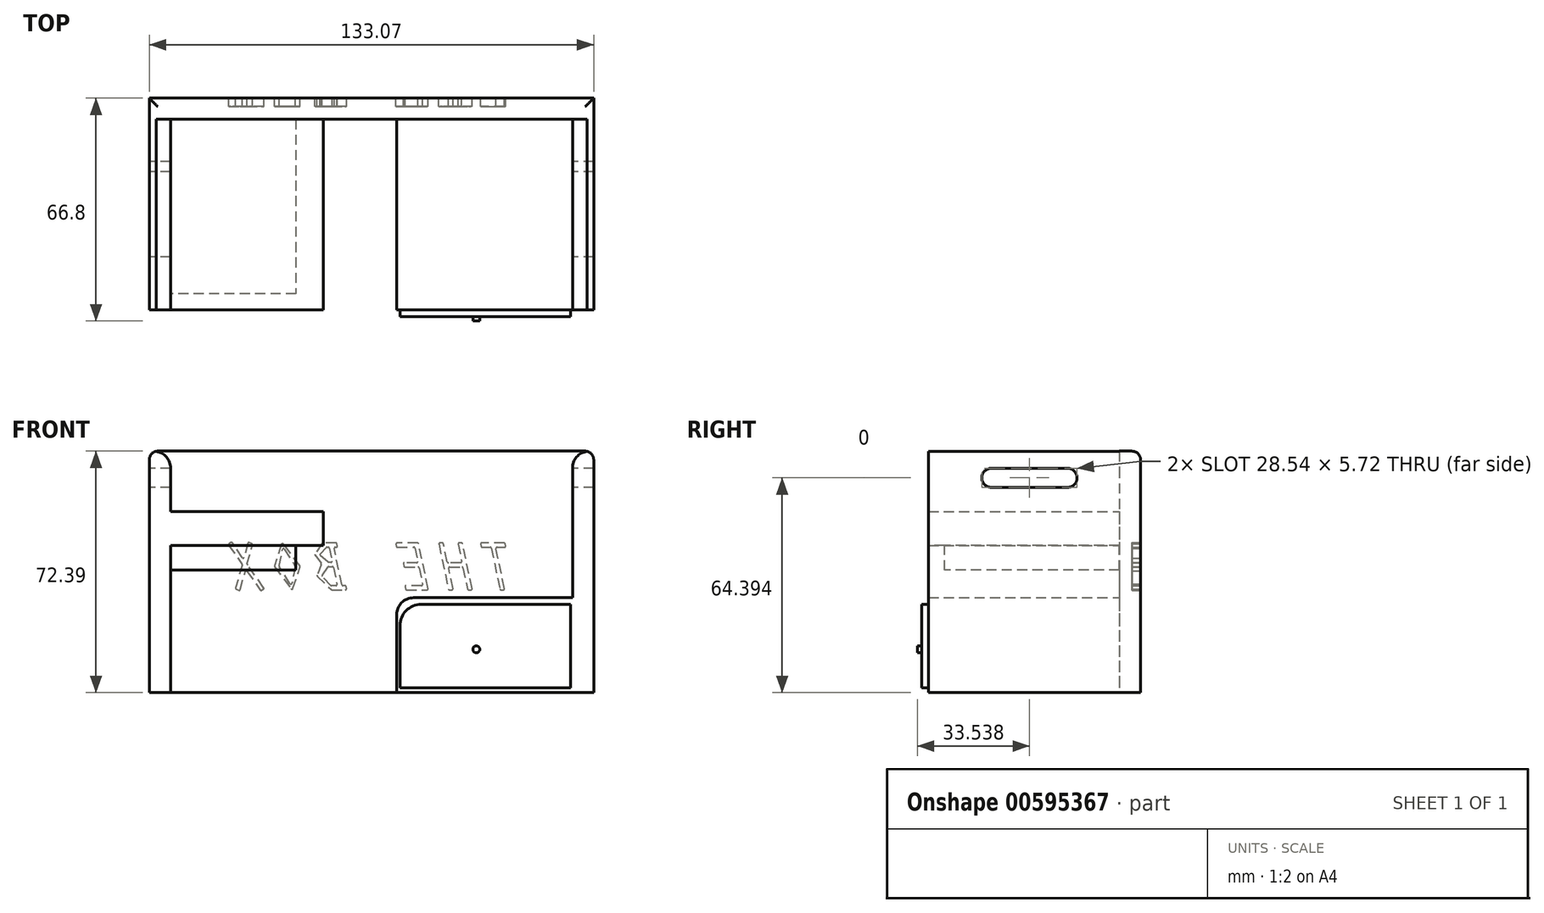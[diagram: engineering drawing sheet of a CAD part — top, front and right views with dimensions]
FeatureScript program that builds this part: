
annotation { "Feature Type Name" : "Feature", "Feature Type Description" : "" }
export const myFeature = defineFeature(function(context is Context, id is Id, definition is map)
    precondition{}
    {
        {
            var Q0;
            Q0=qCreatedBy(makeId("Top.planeOp"),FACE);
            var sketch = newSketch(context, id + "F0", { "sketchPlane" : qUnion([Q0])});
            skLineSegment(sketch, "E0", {"start": v(-65.97, -48.33) * mm, "end": v(-65.97, 15.17) * mm});
            skLineSegment(sketch, "E1", {"start": v(-65.97, 15.17) * mm, "end": v(67.1, 15.17) * mm});
            skLineSegment(sketch, "E2", {"start": v(67.1, 15.17) * mm, "end": v(67.1, -48.33) * mm});
            skLineSegment(sketch, "E3", {"start": v(67.1, -48.33) * mm, "end": v(60.75, -48.33) * mm});
            skLineSegment(sketch, "E4", {"start": v(60.75, -48.33) * mm, "end": v(60.75, 8.82) * mm});
            skLineSegment(sketch, "E5", {"start": v(60.75, 8.82) * mm, "end": v(-59.62, 8.82) * mm});
            skLineSegment(sketch, "E6", {"start": v(-59.62, 8.82) * mm, "end": v(-59.62, -48.33) * mm});
            skLineSegment(sketch, "E7", {"start": v(-59.62, -48.33) * mm, "end": v(-65.97, -48.33) * mm});
            skSolve(sketch);
        }
        {
            var Q0;
            Q0 = qSketchRegion(id + "F0", true);
            extrude(context, id + "F1", {"entities" : qUnion([Q0]), "depth" : 72.39 * mm, "offsetDistance" : 25.4 * mm});
        }
        {
            var Q0;
            Q0=makeQuery(id+"F1.opExtrude","SWEPT_FACE",FACE,{"disambiguationData":[OSD([sQuery(id+"F0.wireOp",EDGE,"E6")])]});
            var sketch = newSketch(context, id + "F2", { "sketchPlane" : qUnion([Q0])});
            skLineSegment(sketch, "E8.bottom", {"start": v(-48.33, 54.32) * mm, "end": v(8.82, 54.32) * mm});
            skLineSegment(sketch, "E8.top", {"start": v(-48.33, 44.07) * mm, "end": v(8.82, 44.07) * mm});
            skLineSegment(sketch, "E8.left", {"start": v(-48.33, 54.32) * mm, "end": v(-48.33, 44.07) * mm});
            skLineSegment(sketch, "E8.right", {"start": v(8.82, 54.32) * mm, "end": v(8.82, 44.07) * mm});
            skSolve(sketch);
        }
        {
            var Q0;
            Q0 = qSketchRegion(id + "F2", true);
            extrude(context, id + "F3", {"entities" : qUnion([Q0]), "operationType" : NewBodyOperationType.ADD, "depth" : 45.72 * mm, "offsetDistance" : 25.4 * mm});
        }
        {
            var Q0;
            Q0=makeQuery(id+"F1.opExtrude","CAP_FACE",FACE,{"disambiguationData":[OSD([sQuery(id+"F0.wireOp",EDGE,"E0"),sQuery(id+"F0.wireOp",EDGE,"E1"),sQuery(id+"F0.wireOp",EDGE,"E2"),sQuery(id+"F0.wireOp",EDGE,"E3"),sQuery(id+"F0.wireOp",EDGE,"E4"),sQuery(id+"F0.wireOp",EDGE,"E5"),sQuery(id+"F0.wireOp",EDGE,"E6"),sQuery(id+"F0.wireOp",EDGE,"E7")])],"isStart":true});
            var sketch = newSketch(context, id + "F4", { "sketchPlane" : qUnion([Q0])});
            skLineSegment(sketch, "E9.bottom", {"start": v(60.75, 48.33) * mm, "end": v(8.08, 48.33) * mm});
            skLineSegment(sketch, "E9.top", {"start": v(60.75, -8.82) * mm, "end": v(8.08, -8.82) * mm});
            skLineSegment(sketch, "E9.left", {"start": v(60.75, 48.33) * mm, "end": v(60.75, -8.82) * mm});
            skLineSegment(sketch, "E9.right", {"start": v(8.08, 48.33) * mm, "end": v(8.08, -8.82) * mm});
            skSolve(sketch);
        }
        {
            var Q0;
            Q0 = qSketchRegion(id + "F4", true);
            extrude(context, id + "F5", {"entities" : qUnion([Q0]), "operationType" : NewBodyOperationType.ADD, "oppositeDirection" : true, "depth" : 28.45 * mm, "offsetDistance" : 25.4 * mm});
        }
        {
            var Q0;
            Q0=makeQuery(id+"F1.opExtrude","CAP_EDGE",EDGE,{"disambiguationData":[OSD([sQuery(id+"F0.wireOp",EDGE,"E6")])],"isStart":false});
            var Q1;
            Q1=makeQuery(id+"F1.opExtrude","CAP_EDGE",EDGE,{"disambiguationData":[OSD([sQuery(id+"F0.wireOp",EDGE,"E4")])],"isStart":false});
            fillet(context, id + "F6", {"entities" : qUnion([Q0, Q1]), "radius" : 5.08 * mm, "tangentPropagation" : true, "allowEdgeOverflow" : false});
        }
        {
            var Q0;
            Q0=makeQuery(id+"F5.opExtrude","CAP_EDGE",EDGE,{"disambiguationData":[OSD([sQuery(id+"F4.wireOp",EDGE,"E9.right")])],"isStart":false});
            fillet(context, id + "F7", {"entities" : qUnion([Q0]), "radius" : 5.08 * mm, "tangentPropagation" : true, "allowEdgeOverflow" : false});
        }
        {
            var Q0;
            Q0=makeQuery(id+"F1.opExtrude","CAP_EDGE",EDGE,{"disambiguationData":[OSD([sQuery(id+"F0.wireOp",EDGE,"E1")])],"isStart":false});
            var Q1;
            Q1=makeQuery(id+"F1.opExtrude","CAP_EDGE",EDGE,{"disambiguationData":[OSD([sQuery(id+"F0.wireOp",EDGE,"E0")])],"isStart":false});
            var Q2;
            Q2=makeQuery(id+"F1.opExtrude","CAP_EDGE",EDGE,{"disambiguationData":[OSD([sQuery(id+"F0.wireOp",EDGE,"E2")])],"isStart":false});
            fillet(context, id + "F8", {"entities" : qUnion([Q0, Q1, Q2]), "radius" : 2.54 * mm, "tangentPropagation" : true, "allowEdgeOverflow" : false});
        }
        {
            var Q0;
            Q0=makeQuery(id+"F5.boolean.opBoolean","MERGE",FACE,{"derivedFrom":[makeQuery(id+"F1.opExtrude","SWEPT_FACE",FACE,{"disambiguationData":[OSD([sQuery(id+"F0.wireOp",EDGE,"E3")])]}),makeQuery(id+"F5.opExtrude","SWEPT_FACE",FACE,{"disambiguationData":[OSD([sQuery(id+"F4.wireOp",EDGE,"E9.bottom")])]})]});
            var sketch = newSketch(context, id + "F9", { "sketchPlane" : qUnion([Q0])});
            skLineSegment(sketch, "E10.bottom", {"start": v(9.09, 1.5) * mm, "end": v(60.22, 1.5) * mm});
            skLineSegment(sketch, "E10.top", {"start": v(15.44, 26.47) * mm, "end": v(60.22, 26.47) * mm});
            skLineSegment(sketch, "E10.left", {"start": v(9.09, 1.5) * mm, "end": v(9.09, 20.12) * mm});
            skLineSegment(sketch, "E10.right", {"start": v(60.22, 1.5) * mm, "end": v(60.22, 26.47) * mm});
            skPoint(sketch, "E11.visualSharp", {"position": v(9.09, 26.47) * mm});
            skArc(sketch, "E11.filletArc", {"start": v(15.44, 26.47) * mm, "mid": v(10.95, 24.6) * mm, "end": v(9.09, 20.12) * mm});
            skSolve(sketch);
        }
        {
            var Q0;
            Q0 = qSketchRegion(id + "F9", true);
            extrude(context, id + "F10", {"entities" : qUnion([Q0]), "operationType" : NewBodyOperationType.ADD, "depth" : 2.03 * mm, "offsetDistance" : 25.4 * mm});
        }
        {
            var Q0;
            Q0=makeQuery(id+"F10.opExtrude","CAP_FACE",FACE,{"disambiguationData":[OSD([sQuery(id+"F9.wireOp",EDGE,"E10.bottom"),sQuery(id+"F9.wireOp",EDGE,"E10.top"),sQuery(id+"F9.wireOp",EDGE,"E10.left"),sQuery(id+"F9.wireOp",EDGE,"E10.right"),sQuery(id+"F9.wireOp",EDGE,"E11.filletArc")])],"isStart":false});
            var sketch = newSketch(context, id + "F11", { "sketchPlane" : qUnion([Q0])});
            skCircle(sketch, "E12", {"center": v(31.95, 12.98) * mm, "radius": 2.13 * mm});
            skCircle(sketch, "E13", {"center": v(31.95, 12.98) * mm, "radius": 1.03 * mm});
            skSolve(sketch);
        }
        {
            var Q0;
            Q0=makeQuery(id+"F11.imprint","IMPRINT",FACE,{"disambiguationData":[TD([[makeQuery(id+"F11.imprint","IMPRINT",EDGE,{"derivedFrom":sQuery(id+"F11.wireOp",EDGE,"E13")}),1.0]])]});
            extrude(context, id + "F12", {"entities" : qUnion([Q0]), "operationType" : NewBodyOperationType.ADD, "depth" : 1.27 * mm, "offsetDistance" : 25.4 * mm});
        }
        {
            var Q0;
            Q0=makeQuery(id+"F3.opExtrude","SWEPT_FACE",FACE,{"disambiguationData":[OSD([sQuery(id+"F2.wireOp",EDGE,"E8.top")])]});
            var sketch = newSketch(context, id + "F13", { "sketchPlane" : qUnion([Q0])});
            skLineSegment(sketch, "E14.bottom", {"start": v(-59.62, -8.82) * mm, "end": v(-22.07, -8.82) * mm});
            skLineSegment(sketch, "E14.top", {"start": v(-59.62, 48.33) * mm, "end": v(-22.07, 48.33) * mm});
            skLineSegment(sketch, "E14.left", {"start": v(-59.62, -8.82) * mm, "end": v(-59.62, 48.33) * mm});
            skLineSegment(sketch, "E14.right", {"start": v(-22.07, -8.82) * mm, "end": v(-22.07, 48.33) * mm});
            skSolve(sketch);
        }
        {
            var Q0;
            Q0 = qSketchRegion(id + "F13", true);
            extrude(context, id + "F14", {"entities" : qUnion([Q0]), "operationType" : NewBodyOperationType.ADD, "depth" : 7.37 * mm, "offsetDistance" : 25.4 * mm});
        }
        {
            var Q0;
            Q0=makeQuery(id+"F14.boolean.opBoolean","MERGE",FACE,{"derivedFrom":[makeQuery(id+"F3.boolean.opBoolean","MERGE",FACE,{"derivedFrom":[makeQuery(id+"F1.opExtrude","SWEPT_FACE",FACE,{"disambiguationData":[OSD([sQuery(id+"F0.wireOp",EDGE,"E7")])]}),makeQuery(id+"F3.opExtrude","SWEPT_FACE",FACE,{"disambiguationData":[OSD([sQuery(id+"F2.wireOp",EDGE,"E8.left")])]})]}),makeQuery(id+"F14.opExtrude","SWEPT_FACE",FACE,{"disambiguationData":[OSD([sQuery(id+"F13.wireOp",EDGE,"E14.top")])]})]});
            var sketch = newSketch(context, id + "F15", { "sketchPlane" : qUnion([Q0])});
            skPoint(sketch, "E15.oppositeSnap0", {"position": v(-17.98, 44.07) * mm});
            skLineSegment(sketch, "E15.bottom", {"start": v(-22.07, 36.7) * mm, "end": v(-59.62, 36.7) * mm});
            skLineSegment(sketch, "E15.top", {"start": v(-22.07, 44.07) * mm, "end": v(-59.62, 44.07) * mm});
            skLineSegment(sketch, "E15.left", {"start": v(-22.07, 36.7) * mm, "end": v(-22.07, 44.07) * mm});
            skLineSegment(sketch, "E15.right", {"start": v(-59.62, 36.7) * mm, "end": v(-59.62, 44.07) * mm});
            skSolve(sketch);
        }
        {
            var Q0;
            Q0=makeQuery(id+"F15.imprint","IMPRINT",FACE,{"disambiguationData":[TD([[makeQuery(id+"F15.imprint","IMPRINT",EDGE,{"derivedFrom":sQuery(id+"F15.wireOp",EDGE,"E15.bottom")}),-1.0]])]});
            extrude(context, id + "F16", {"entities" : qUnion([Q0]), "operationType" : NewBodyOperationType.REMOVE, "oppositeDirection" : true, "depth" : 4.83 * mm, "offsetDistance" : 25.4 * mm});
        }
        {
            var Q0;
            Q0=makeQuery(id+"F1.opExtrude","SWEPT_FACE",FACE,{"disambiguationData":[OSD([sQuery(id+"F0.wireOp",EDGE,"E0")])]});
            var sketch = newSketch(context, id + "F17", { "sketchPlane" : qUnion([Q0])});
            skArc(sketch, "E16", {"start": v(6.82, 67.25) * mm, "mid": v(3.82, 64.47) * mm, "end": v(6.68, 61.54) * mm});
            skArc(sketch, "E17", {"start": v(29.5, 61.54) * mm, "mid": v(32.36, 64.4) * mm, "end": v(29.5, 67.25) * mm});
            skLineSegment(sketch, "E18", {"start": v(6.53, 67.25) * mm, "end": v(29.5, 67.25) * mm});
            skLineSegment(sketch, "E19", {"start": v(6.68, 61.54) * mm, "end": v(29.5, 61.54) * mm});
            skSolve(sketch);
        }
        {
            var Q0;
            Q0 = qSketchRegion(id + "F17", true);
            extrude(context, id + "F18", {"entities" : qUnion([Q0]), "operationType" : NewBodyOperationType.REMOVE, "endBound" : BoundingType.THROUGH_ALL, "oppositeDirection" : true, "depth" : 25.4 * mm, "offsetDistance" : 25.4 * mm});
        }
        {
            var Q0;
            Q0=makeQuery(id+"F1.opExtrude","SWEPT_FACE",FACE,{"disambiguationData":[OSD([sQuery(id+"F0.wireOp",EDGE,"E1")])]});
            var sketch = newSketch(context, id + "F19", { "sketchPlane" : qUnion([Q0])});
            skLineSegment(sketch, "E20", {"start": v(-38.18, 43.6) * mm, "end": v(-40.4, 43.6) * mm});
            skLineSegment(sketch, "E21", {"start": v(-40.72, 43.98) * mm, "end": v(-40.59, 44.6) * mm});
            skLineSegment(sketch, "E22", {"start": v(-40.27, 44.86) * mm, "end": v(-33.54, 44.86) * mm});
            skLineSegment(sketch, "E23", {"start": v(-33.22, 44.47) * mm, "end": v(-33.36, 43.85) * mm});
            skLineSegment(sketch, "E24", {"start": v(-33.67, 43.6) * mm, "end": v(-36.11, 43.6) * mm});
            skLineSegment(sketch, "E25", {"start": v(-36.43, 43.34) * mm, "end": v(-39.03, 31.1) * mm});
            skLineSegment(sketch, "E26", {"start": v(-39.34, 30.85) * mm, "end": v(-40.1, 30.85) * mm});
            skLineSegment(sketch, "E27", {"start": v(-40.4, 31.23) * mm, "end": v(-37.86, 43.2) * mm});
            skLineSegment(sketch, "E28", {"start": v(-27.54, 44.86) * mm, "end": v(-26.8, 44.86) * mm});
            skLineSegment(sketch, "E29", {"start": v(-26.48, 44.47) * mm, "end": v(-27.57, 39.36) * mm});
            skLineSegment(sketch, "E30", {"start": v(-27.26, 38.98) * mm, "end": v(-23.59, 38.98) * mm});
            skLineSegment(sketch, "E31", {"start": v(-23.28, 39.23) * mm, "end": v(-22.12, 44.6) * mm});
            skLineSegment(sketch, "E32", {"start": v(-21.81, 44.86) * mm, "end": v(-21.06, 44.86) * mm});
            skLineSegment(sketch, "E33", {"start": v(-20.74, 44.47) * mm, "end": v(-23.6, 31.1) * mm});
            skLineSegment(sketch, "E34", {"start": v(-23.9, 30.85) * mm, "end": v(-24.66, 30.85) * mm});
            skLineSegment(sketch, "E35", {"start": v(-24.97, 31.23) * mm, "end": v(-23.67, 37.33) * mm});
            skLineSegment(sketch, "E36", {"start": v(-23.98, 37.72) * mm, "end": v(-27.65, 37.72) * mm});
            skLineSegment(sketch, "E37", {"start": v(-27.96, 37.46) * mm, "end": v(-29.32, 31.1) * mm});
            skLineSegment(sketch, "E38", {"start": v(-29.64, 30.85) * mm, "end": v(-30.4, 30.85) * mm});
            skLineSegment(sketch, "E39", {"start": v(-30.7, 31.23) * mm, "end": v(-27.86, 44.6) * mm});
            skLineSegment(sketch, "E40", {"start": v(-14.38, 44.86) * mm, "end": v(-8.2, 44.86) * mm});
            skLineSegment(sketch, "E41", {"start": v(-7.9, 44.47) * mm, "end": v(-8.03, 43.85) * mm});
            skLineSegment(sketch, "E42", {"start": v(-8.34, 43.6) * mm, "end": v(-13.24, 43.6) * mm});
            skLineSegment(sketch, "E43", {"start": v(-13.56, 43.34) * mm, "end": v(-14.4, 39.36) * mm});
            skLineSegment(sketch, "E44", {"start": v(-14.1, 38.98) * mm, "end": v(-10.4, 38.98) * mm});
            skLineSegment(sketch, "E45", {"start": v(-10.1, 38.6) * mm, "end": v(-10.21, 37.97) * mm});
            skLineSegment(sketch, "E46", {"start": v(-10.53, 37.72) * mm, "end": v(-14.48, 37.72) * mm});
            skLineSegment(sketch, "E47", {"start": v(-14.8, 37.46) * mm, "end": v(-15.85, 32.5) * mm});
            skLineSegment(sketch, "E48", {"start": v(-15.54, 32.1) * mm, "end": v(-10.92, 32.1) * mm});
            skLineSegment(sketch, "E49", {"start": v(-10.6, 31.72) * mm, "end": v(-10.74, 31.1) * mm});
            skLineSegment(sketch, "E50", {"start": v(-11.05, 30.85) * mm, "end": v(-17.22, 30.85) * mm});
            skLineSegment(sketch, "E51", {"start": v(-17.54, 31.23) * mm, "end": v(-14.69, 44.6) * mm});
            skLineSegment(sketch, "E52", {"start": v(6.93, 31.24) * mm, "end": v(7.07, 31.85) * mm});
            skLineSegment(sketch, "E53", {"start": v(7.38, 32.1) * mm, "end": v(8, 32.1) * mm});
            skLineSegment(sketch, "E54", {"start": v(8.31, 32.36) * mm, "end": v(10.61, 43.2) * mm});
            skLineSegment(sketch, "E55", {"start": v(10.3, 43.6) * mm, "end": v(9.96, 43.6) * mm});
            skLineSegment(sketch, "E56", {"start": v(9.64, 43.98) * mm, "end": v(9.78, 44.6) * mm});
            skLineSegment(sketch, "E57", {"start": v(10.1, 44.86) * mm, "end": v(13.95, 44.86) * mm});
            skLineSegment(sketch, "E58", {"start": v(14.21, 44.71) * mm, "end": v(16.34, 41.52) * mm});
            skLineSegment(sketch, "E59", {"start": v(16.33, 41.15) * mm, "end": v(14.52, 38.76) * mm});
            skLineSegment(sketch, "E60", {"start": v(14.48, 38.45) * mm, "end": v(15.72, 35.25) * mm});
            skLineSegment(sketch, "E61", {"start": v(15.64, 34.9) * mm, "end": v(11.46, 30.93) * mm});
            skLineSegment(sketch, "E62", {"start": v(11.24, 30.85) * mm, "end": v(7.25, 30.85) * mm});
            skLineSegment(sketch, "E63", {"start": v(11.67, 32.2) * mm, "end": v(14.15, 34.88) * mm});
            skLineSegment(sketch, "E64", {"start": v(14.18, 35.28) * mm, "end": v(12.51, 37.7) * mm});
            skLineSegment(sketch, "E65", {"start": v(12.25, 37.84) * mm, "end": v(11.14, 37.84) * mm});
            skLineSegment(sketch, "E66", {"start": v(10.83, 37.59) * mm, "end": v(9.75, 32.5) * mm});
            skLineSegment(sketch, "E67", {"start": v(10.06, 32.1) * mm, "end": v(11.44, 32.1) * mm});
            skLineSegment(sketch, "E68", {"start": v(12.5, 39.18) * mm, "end": v(14.75, 41.11) * mm});
            skLineSegment(sketch, "E69", {"start": v(14.78, 41.57) * mm, "end": v(13.02, 43.5) * mm});
            skLineSegment(sketch, "E70", {"start": v(12.78, 43.6) * mm, "end": v(12.36, 43.6) * mm});
            skLineSegment(sketch, "E71", {"start": v(12.05, 43.34) * mm, "end": v(11.24, 39.49) * mm});
            skLineSegment(sketch, "E72", {"start": v(11.55, 39.1) * mm, "end": v(12.3, 39.1) * mm});
            skLineSegment(sketch, "E73", {"start": v(28.47, 37.73) * mm, "end": v(23.52, 31.15) * mm});
            skLineSegment(sketch, "E74", {"start": v(22.96, 31.24) * mm, "end": v(20.85, 37.7) * mm});
            skLineSegment(sketch, "E75", {"start": v(20.9, 38) * mm, "end": v(25.85, 44.56) * mm});
            skLineSegment(sketch, "E76", {"start": v(26.4, 44.46) * mm, "end": v(28.52, 38.02) * mm});
            skLineSegment(sketch, "E77", {"start": v(22.3, 37.74) * mm, "end": v(23.26, 32.78) * mm});
            skLineSegment(sketch, "E78", {"start": v(23.85, 32.67) * mm, "end": v(27.03, 37.75) * mm});
            skLineSegment(sketch, "E79", {"start": v(27.07, 37.99) * mm, "end": v(26.08, 42.93) * mm});
            skLineSegment(sketch, "E80", {"start": v(25.5, 43.04) * mm, "end": v(22.33, 37.97) * mm});
            skLineSegment(sketch, "E81", {"start": v(32.4, 30.7) * mm, "end": v(31.83, 31) * mm});
            skLineSegment(sketch, "E82", {"start": v(31.72, 31.46) * mm, "end": v(36.63, 38.35) * mm});
            skLineSegment(sketch, "E83", {"start": v(36.67, 38.62) * mm, "end": v(35.07, 44.21) * mm});
            skLineSegment(sketch, "E84", {"start": v(35.25, 44.6) * mm, "end": v(36.1, 44.97) * mm});
            skLineSegment(sketch, "E85", {"start": v(36.53, 44.76) * mm, "end": v(37.55, 40.6) * mm});
            skLineSegment(sketch, "E86", {"start": v(38.13, 40.5) * mm, "end": v(41.07, 44.88) * mm});
            skLineSegment(sketch, "E87", {"start": v(41.5, 44.98) * mm, "end": v(42.08, 44.65) * mm});
            skLineSegment(sketch, "E88", {"start": v(42.18, 44.19) * mm, "end": v(38.2, 38.6) * mm});
            skLineSegment(sketch, "E89", {"start": v(38.15, 38.32) * mm, "end": v(40.12, 31.43) * mm});
            skLineSegment(sketch, "E90", {"start": v(39.94, 31.05) * mm, "end": v(39.16, 30.72) * mm});
            skLineSegment(sketch, "E91", {"start": v(38.72, 30.93) * mm, "end": v(37.3, 36.31) * mm});
            skLineSegment(sketch, "E92", {"start": v(36.72, 36.41) * mm, "end": v(32.8, 30.8) * mm});
            skPoint(sketch, "E93.visualSharp", {"position": v(-40.53, 44.86) * mm});
            skArc(sketch, "E93.filletArc", {"start": v(-40.27, 44.86) * mm, "mid": v(-40.47, 44.79) * mm, "end": v(-40.59, 44.6) * mm});
            skPoint(sketch, "E94.visualSharp", {"position": v(-40.8, 43.6) * mm});
            skArc(sketch, "E94.filletArc", {"start": v(-40.72, 43.98) * mm, "mid": v(-40.66, 43.72) * mm, "end": v(-40.4, 43.6) * mm});
            skPoint(sketch, "E95.visualSharp", {"position": v(-37.78, 43.6) * mm});
            skArc(sketch, "E95.filletArc", {"start": v(-37.86, 43.2) * mm, "mid": v(-37.93, 43.48) * mm, "end": v(-38.18, 43.6) * mm});
            skPoint(sketch, "E96.visualSharp", {"position": v(-36.37, 43.6) * mm});
            skArc(sketch, "E96.filletArc", {"start": v(-36.11, 43.6) * mm, "mid": v(-36.31, 43.52) * mm, "end": v(-36.43, 43.34) * mm});
            skPoint(sketch, "E97.visualSharp", {"position": v(-33.41, 43.6) * mm});
            skArc(sketch, "E97.filletArc", {"start": v(-33.67, 43.6) * mm, "mid": v(-33.47, 43.67) * mm, "end": v(-33.36, 43.85) * mm});
            skPoint(sketch, "E98.visualSharp", {"position": v(-33.14, 44.86) * mm});
            skArc(sketch, "E98.filletArc", {"start": v(-33.22, 44.47) * mm, "mid": v(-33.29, 44.74) * mm, "end": v(-33.54, 44.86) * mm});
            skPoint(sketch, "E99.visualSharp", {"position": v(-40.49, 30.85) * mm});
            skArc(sketch, "E99.filletArc", {"start": v(-40.4, 31.23) * mm, "mid": v(-40.34, 30.97) * mm, "end": v(-40.1, 30.85) * mm});
            skPoint(sketch, "E100.visualSharp", {"position": v(-39.08, 30.85) * mm});
            skArc(sketch, "E100.filletArc", {"start": v(-39.34, 30.85) * mm, "mid": v(-39.14, 30.92) * mm, "end": v(-39.03, 31.1) * mm});
            skPoint(sketch, "E101.visualSharp", {"position": v(-30.79, 30.85) * mm});
            skArc(sketch, "E101.filletArc", {"start": v(-30.7, 31.23) * mm, "mid": v(-30.64, 30.97) * mm, "end": v(-30.4, 30.85) * mm});
            skPoint(sketch, "E102.visualSharp", {"position": v(-29.38, 30.85) * mm});
            skArc(sketch, "E102.filletArc", {"start": v(-29.64, 30.85) * mm, "mid": v(-29.44, 30.92) * mm, "end": v(-29.32, 31.1) * mm});
            skPoint(sketch, "E103.visualSharp", {"position": v(-27.9, 37.72) * mm});
            skArc(sketch, "E103.filletArc", {"start": v(-27.65, 37.72) * mm, "mid": v(-27.85, 37.64) * mm, "end": v(-27.96, 37.46) * mm});
            skPoint(sketch, "E104.visualSharp", {"position": v(-27.66, 38.98) * mm});
            skArc(sketch, "E104.filletArc", {"start": v(-27.57, 39.36) * mm, "mid": v(-27.5, 39.1) * mm, "end": v(-27.26, 38.98) * mm});
            skPoint(sketch, "E105.visualSharp", {"position": v(-27.8, 44.86) * mm});
            skArc(sketch, "E105.filletArc", {"start": v(-27.54, 44.86) * mm, "mid": v(-27.75, 44.79) * mm, "end": v(-27.86, 44.6) * mm});
            skPoint(sketch, "E106.visualSharp", {"position": v(-26.4, 44.86) * mm});
            skArc(sketch, "E106.filletArc", {"start": v(-26.48, 44.47) * mm, "mid": v(-26.54, 44.74) * mm, "end": v(-26.8, 44.86) * mm});
            skPoint(sketch, "E107.visualSharp", {"position": v(-23.33, 38.98) * mm});
            skArc(sketch, "E107.filletArc", {"start": v(-23.59, 38.98) * mm, "mid": v(-23.39, 39.05) * mm, "end": v(-23.28, 39.23) * mm});
            skPoint(sketch, "E108.visualSharp", {"position": v(-22.07, 44.86) * mm});
            skArc(sketch, "E108.filletArc", {"start": v(-21.81, 44.86) * mm, "mid": v(-22.01, 44.79) * mm, "end": v(-22.12, 44.6) * mm});
            skPoint(sketch, "E109.visualSharp", {"position": v(-20.66, 44.86) * mm});
            skArc(sketch, "E109.filletArc", {"start": v(-20.74, 44.47) * mm, "mid": v(-20.8, 44.74) * mm, "end": v(-21.06, 44.86) * mm});
            skPoint(sketch, "E110.visualSharp", {"position": v(-23.58, 37.72) * mm});
            skArc(sketch, "E110.filletArc", {"start": v(-23.67, 37.33) * mm, "mid": v(-23.73, 37.6) * mm, "end": v(-23.98, 37.72) * mm});
            skPoint(sketch, "E111.visualSharp", {"position": v(-25.05, 30.85) * mm});
            skArc(sketch, "E111.filletArc", {"start": v(-24.97, 31.23) * mm, "mid": v(-24.9, 30.97) * mm, "end": v(-24.66, 30.85) * mm});
            skPoint(sketch, "E112.visualSharp", {"position": v(-23.64, 30.85) * mm});
            skArc(sketch, "E112.filletArc", {"start": v(-23.9, 30.85) * mm, "mid": v(-23.7, 30.92) * mm, "end": v(-23.6, 31.1) * mm});
            skPoint(sketch, "E113.visualSharp", {"position": v(-17.62, 30.85) * mm});
            skArc(sketch, "E113.filletArc", {"start": v(-17.54, 31.23) * mm, "mid": v(-17.47, 30.97) * mm, "end": v(-17.22, 30.85) * mm});
            skPoint(sketch, "E114.visualSharp", {"position": v(-10.8, 30.85) * mm});
            skArc(sketch, "E114.filletArc", {"start": v(-11.05, 30.85) * mm, "mid": v(-10.85, 30.92) * mm, "end": v(-10.74, 31.1) * mm});
            skPoint(sketch, "E115.visualSharp", {"position": v(-10.52, 32.1) * mm});
            skArc(sketch, "E115.filletArc", {"start": v(-10.6, 31.72) * mm, "mid": v(-10.67, 31.99) * mm, "end": v(-10.92, 32.1) * mm});
            skPoint(sketch, "E116.visualSharp", {"position": v(-15.94, 32.1) * mm});
            skArc(sketch, "E116.filletArc", {"start": v(-15.85, 32.5) * mm, "mid": v(-15.8, 32.23) * mm, "end": v(-15.54, 32.1) * mm});
            skPoint(sketch, "E117.visualSharp", {"position": v(-14.74, 37.72) * mm});
            skArc(sketch, "E117.filletArc", {"start": v(-14.48, 37.72) * mm, "mid": v(-14.68, 37.64) * mm, "end": v(-14.8, 37.46) * mm});
            skPoint(sketch, "E118.visualSharp", {"position": v(-10.27, 37.72) * mm});
            skArc(sketch, "E118.filletArc", {"start": v(-10.53, 37.72) * mm, "mid": v(-10.33, 37.79) * mm, "end": v(-10.21, 37.97) * mm});
            skPoint(sketch, "E119.visualSharp", {"position": v(-10.01, 38.98) * mm});
            skArc(sketch, "E119.filletArc", {"start": v(-10.1, 38.6) * mm, "mid": v(-10.16, 38.86) * mm, "end": v(-10.4, 38.98) * mm});
            skPoint(sketch, "E120.visualSharp", {"position": v(-14.49, 38.98) * mm});
            skArc(sketch, "E120.filletArc", {"start": v(-14.4, 39.36) * mm, "mid": v(-14.34, 39.1) * mm, "end": v(-14.1, 38.98) * mm});
            skPoint(sketch, "E121.visualSharp", {"position": v(-13.5, 43.6) * mm});
            skArc(sketch, "E121.filletArc", {"start": v(-13.24, 43.6) * mm, "mid": v(-13.44, 43.52) * mm, "end": v(-13.56, 43.34) * mm});
            skPoint(sketch, "E122.visualSharp", {"position": v(-8.08, 43.6) * mm});
            skArc(sketch, "E122.filletArc", {"start": v(-8.34, 43.6) * mm, "mid": v(-8.14, 43.67) * mm, "end": v(-8.03, 43.85) * mm});
            skPoint(sketch, "E123.visualSharp", {"position": v(-7.8, 44.86) * mm});
            skArc(sketch, "E123.filletArc", {"start": v(-7.9, 44.47) * mm, "mid": v(-7.96, 44.74) * mm, "end": v(-8.2, 44.86) * mm});
            skPoint(sketch, "E124.visualSharp", {"position": v(-14.64, 44.86) * mm});
            skArc(sketch, "E124.filletArc", {"start": v(-14.38, 44.86) * mm, "mid": v(-14.58, 44.79) * mm, "end": v(-14.69, 44.6) * mm});
            skPoint(sketch, "E125.visualSharp", {"position": v(9.83, 44.86) * mm});
            skArc(sketch, "E125.filletArc", {"start": v(10.1, 44.86) * mm, "mid": v(9.89, 44.79) * mm, "end": v(9.78, 44.6) * mm});
            skPoint(sketch, "E126.visualSharp", {"position": v(9.56, 43.6) * mm});
            skArc(sketch, "E126.filletArc", {"start": v(9.64, 43.98) * mm, "mid": v(9.7, 43.72) * mm, "end": v(9.96, 43.6) * mm});
            skPoint(sketch, "E127.visualSharp", {"position": v(10.7, 43.6) * mm});
            skArc(sketch, "E127.filletArc", {"start": v(10.61, 43.2) * mm, "mid": v(10.55, 43.48) * mm, "end": v(10.3, 43.6) * mm});
            skPoint(sketch, "E128.visualSharp", {"position": v(12.92, 43.6) * mm});
            skArc(sketch, "E128.filletArc", {"start": v(13.02, 43.5) * mm, "mid": v(12.9, 43.57) * mm, "end": v(12.78, 43.6) * mm});
            skPoint(sketch, "E129.visualSharp", {"position": v(12.1, 43.6) * mm});
            skArc(sketch, "E129.filletArc", {"start": v(12.36, 43.6) * mm, "mid": v(12.16, 43.52) * mm, "end": v(12.05, 43.34) * mm});
            skPoint(sketch, "E130.visualSharp", {"position": v(11.16, 39.1) * mm});
            skArc(sketch, "E130.filletArc", {"start": v(11.24, 39.49) * mm, "mid": v(11.3, 39.22) * mm, "end": v(11.55, 39.1) * mm});
            skPoint(sketch, "E131.visualSharp", {"position": v(12.42, 39.1) * mm});
            skArc(sketch, "E131.filletArc", {"start": v(12.3, 39.1) * mm, "mid": v(12.4, 39.12) * mm, "end": v(12.5, 39.18) * mm});
            skPoint(sketch, "E132.visualSharp", {"position": v(15, 41.33) * mm});
            skArc(sketch, "E132.filletArc", {"start": v(14.75, 41.11) * mm, "mid": v(14.86, 41.34) * mm, "end": v(14.78, 41.57) * mm});
            skPoint(sketch, "E133.visualSharp", {"position": v(14.12, 44.86) * mm});
            skArc(sketch, "E133.filletArc", {"start": v(14.21, 44.71) * mm, "mid": v(14.1, 44.82) * mm, "end": v(13.95, 44.86) * mm});
            skPoint(sketch, "E134.visualSharp", {"position": v(16.47, 41.33) * mm});
            skArc(sketch, "E134.filletArc", {"start": v(16.33, 41.15) * mm, "mid": v(16.4, 41.33) * mm, "end": v(16.34, 41.52) * mm});
            skPoint(sketch, "E135.visualSharp", {"position": v(14.41, 38.62) * mm});
            skArc(sketch, "E135.filletArc", {"start": v(14.52, 38.76) * mm, "mid": v(14.46, 38.61) * mm, "end": v(14.48, 38.45) * mm});
            skPoint(sketch, "E136.visualSharp", {"position": v(15.8, 35.05) * mm});
            skArc(sketch, "E136.filletArc", {"start": v(15.64, 34.9) * mm, "mid": v(15.73, 35.06) * mm, "end": v(15.72, 35.25) * mm});
            skPoint(sketch, "E137.visualSharp", {"position": v(11.37, 30.85) * mm});
            skArc(sketch, "E137.filletArc", {"start": v(11.24, 30.85) * mm, "mid": v(11.36, 30.87) * mm, "end": v(11.46, 30.93) * mm});
            skPoint(sketch, "E138.visualSharp", {"position": v(6.85, 30.85) * mm});
            skArc(sketch, "E138.filletArc", {"start": v(6.93, 31.24) * mm, "mid": v(7, 30.97) * mm, "end": v(7.25, 30.85) * mm});
            skPoint(sketch, "E139.visualSharp", {"position": v(7.12, 32.1) * mm});
            skArc(sketch, "E139.filletArc", {"start": v(7.38, 32.1) * mm, "mid": v(7.18, 32.04) * mm, "end": v(7.07, 31.85) * mm});
            skPoint(sketch, "E140.visualSharp", {"position": v(8.26, 32.1) * mm});
            skArc(sketch, "E140.filletArc", {"start": v(8, 32.1) * mm, "mid": v(8.2, 32.18) * mm, "end": v(8.31, 32.36) * mm});
            skPoint(sketch, "E141.visualSharp", {"position": v(9.66, 32.1) * mm});
            skArc(sketch, "E141.filletArc", {"start": v(9.75, 32.5) * mm, "mid": v(9.81, 32.23) * mm, "end": v(10.06, 32.1) * mm});
            skPoint(sketch, "E142.visualSharp", {"position": v(11.58, 32.1) * mm});
            skArc(sketch, "E142.filletArc", {"start": v(11.44, 32.1) * mm, "mid": v(11.56, 32.13) * mm, "end": v(11.67, 32.2) * mm});
            skPoint(sketch, "E143.visualSharp", {"position": v(14.33, 35.07) * mm});
            skArc(sketch, "E143.filletArc", {"start": v(14.15, 34.88) * mm, "mid": v(14.24, 35.08) * mm, "end": v(14.18, 35.28) * mm});
            skPoint(sketch, "E144.visualSharp", {"position": v(12.42, 37.84) * mm});
            skArc(sketch, "E144.filletArc", {"start": v(12.51, 37.7) * mm, "mid": v(12.4, 37.8) * mm, "end": v(12.25, 37.84) * mm});
            skPoint(sketch, "E145.visualSharp", {"position": v(10.88, 37.84) * mm});
            skArc(sketch, "E145.filletArc", {"start": v(11.14, 37.84) * mm, "mid": v(10.94, 37.77) * mm, "end": v(10.83, 37.59) * mm});
            skPoint(sketch, "E146.visualSharp", {"position": v(23.15, 30.66) * mm});
            skArc(sketch, "E146.filletArc", {"start": v(22.96, 31.24) * mm, "mid": v(23.2, 31.03) * mm, "end": v(23.52, 31.15) * mm});
            skPoint(sketch, "E147.visualSharp", {"position": v(23.42, 31.98) * mm});
            skArc(sketch, "E147.filletArc", {"start": v(23.26, 32.78) * mm, "mid": v(23.52, 32.52) * mm, "end": v(23.85, 32.67) * mm});
            skPoint(sketch, "E148.visualSharp", {"position": v(22.27, 37.86) * mm});
            skArc(sketch, "E148.filletArc", {"start": v(22.33, 37.97) * mm, "mid": v(22.29, 37.86) * mm, "end": v(22.3, 37.74) * mm});
            skPoint(sketch, "E149.visualSharp", {"position": v(20.8, 37.86) * mm});
            skArc(sketch, "E149.filletArc", {"start": v(20.9, 38) * mm, "mid": v(20.84, 37.86) * mm, "end": v(20.85, 37.7) * mm});
            skPoint(sketch, "E150.visualSharp", {"position": v(27.1, 37.86) * mm});
            skArc(sketch, "E150.filletArc", {"start": v(27.03, 37.75) * mm, "mid": v(27.07, 37.87) * mm, "end": v(27.07, 37.99) * mm});
            skPoint(sketch, "E151.visualSharp", {"position": v(28.57, 37.86) * mm});
            skArc(sketch, "E151.filletArc", {"start": v(28.47, 37.73) * mm, "mid": v(28.53, 37.87) * mm, "end": v(28.52, 38.02) * mm});
            skPoint(sketch, "E152.visualSharp", {"position": v(25.92, 43.72) * mm});
            skArc(sketch, "E152.filletArc", {"start": v(26.08, 42.93) * mm, "mid": v(25.82, 43.18) * mm, "end": v(25.5, 43.04) * mm});
            skPoint(sketch, "E153.visualSharp", {"position": v(26.21, 45.05) * mm});
            skArc(sketch, "E153.filletArc", {"start": v(26.4, 44.46) * mm, "mid": v(26.15, 44.68) * mm, "end": v(25.85, 44.56) * mm});
            skPoint(sketch, "E154.visualSharp", {"position": v(35, 44.48) * mm});
            skArc(sketch, "E154.filletArc", {"start": v(35.25, 44.6) * mm, "mid": v(35.09, 44.43) * mm, "end": v(35.07, 44.21) * mm});
            skPoint(sketch, "E155.visualSharp", {"position": v(36.44, 45.13) * mm});
            skArc(sketch, "E155.filletArc", {"start": v(36.53, 44.76) * mm, "mid": v(36.36, 44.97) * mm, "end": v(36.1, 44.97) * mm});
            skPoint(sketch, "E156.visualSharp", {"position": v(37.72, 39.9) * mm});
            skArc(sketch, "E156.filletArc", {"start": v(37.55, 40.6) * mm, "mid": v(37.8, 40.37) * mm, "end": v(38.13, 40.5) * mm});
            skPoint(sketch, "E157.visualSharp", {"position": v(41.23, 45.13) * mm});
            skArc(sketch, "E157.filletArc", {"start": v(41.5, 44.98) * mm, "mid": v(41.26, 45.02) * mm, "end": v(41.07, 44.88) * mm});
            skPoint(sketch, "E158.visualSharp", {"position": v(42.39, 44.48) * mm});
            skArc(sketch, "E158.filletArc", {"start": v(42.18, 44.19) * mm, "mid": v(42.23, 44.44) * mm, "end": v(42.08, 44.65) * mm});
            skPoint(sketch, "E159.visualSharp", {"position": v(38.1, 38.47) * mm});
            skArc(sketch, "E159.filletArc", {"start": v(38.2, 38.6) * mm, "mid": v(38.14, 38.47) * mm, "end": v(38.15, 38.32) * mm});
            skPoint(sketch, "E160.visualSharp", {"position": v(36.72, 38.47) * mm});
            skArc(sketch, "E160.filletArc", {"start": v(36.63, 38.35) * mm, "mid": v(36.68, 38.48) * mm, "end": v(36.67, 38.62) * mm});
            skPoint(sketch, "E161.visualSharp", {"position": v(37.12, 36.98) * mm});
            skArc(sketch, "E161.filletArc", {"start": v(37.3, 36.31) * mm, "mid": v(37.04, 36.55) * mm, "end": v(36.72, 36.41) * mm});
            skPoint(sketch, "E162.visualSharp", {"position": v(32.64, 30.57) * mm});
            skArc(sketch, "E162.filletArc", {"start": v(32.4, 30.7) * mm, "mid": v(32.62, 30.68) * mm, "end": v(32.8, 30.8) * mm});
            skPoint(sketch, "E163.visualSharp", {"position": v(31.5, 31.16) * mm});
            skArc(sketch, "E163.filletArc", {"start": v(31.72, 31.46) * mm, "mid": v(31.67, 31.2) * mm, "end": v(31.83, 31) * mm});
            skPoint(sketch, "E164.visualSharp", {"position": v(38.82, 30.57) * mm});
            skArc(sketch, "E164.filletArc", {"start": v(38.72, 30.93) * mm, "mid": v(38.9, 30.73) * mm, "end": v(39.16, 30.72) * mm});
            skPoint(sketch, "E165.visualSharp", {"position": v(40.2, 31.16) * mm});
            skArc(sketch, "E165.filletArc", {"start": v(39.94, 31.05) * mm, "mid": v(40.1, 31.2) * mm, "end": v(40.12, 31.43) * mm});
            skSolve(sketch);
        }
        {
            var Q0;
            Q0 = qSketchRegion(id + "F19", true);
            var Q1;
            Q1=sQuery(id+"F19.wireOp",EDGE,"E29");
            var Q2;
            Q2=sQuery(id+"F19.wireOp",EDGE,"E30");
            var Q3;
            Q3=sQuery(id+"F19.wireOp",EDGE,"E31");
            var Q4;
            Q4=sQuery(id+"F19.wireOp",EDGE,"E27");
            var Q5;
            Q5=sQuery(id+"F19.wireOp",EDGE,"E25");
            var Q6;
            Q6=sQuery(id+"F19.wireOp",EDGE,"E24");
            var Q7;
            Q7=sQuery(id+"F19.wireOp",EDGE,"E22");
            var Q8;
            Q8=sQuery(id+"F19.wireOp",EDGE,"E20");
            var Q9;
            Q9=sQuery(id+"F19.wireOp",EDGE,"E35");
            var Q10;
            Q10=sQuery(id+"F19.wireOp",EDGE,"E33");
            var Q11;
            Q11=sQuery(id+"F19.wireOp",EDGE,"E83");
            var Q12;
            Q12=sQuery(id+"F19.wireOp",EDGE,"E51");
            var Q13;
            Q13=sQuery(id+"F19.wireOp",EDGE,"E42");
            var Q14;
            Q14=sQuery(id+"F19.wireOp",EDGE,"E58");
            var Q15;
            Q15=sQuery(id+"F19.wireOp",EDGE,"E67");
            var Q16;
            Q16=sQuery(id+"F19.wireOp",EDGE,"E74");
            var Q17;
            Q17=sQuery(id+"F19.wireOp",EDGE,"E64");
            var Q18;
            Q18=sQuery(id+"F19.wireOp",EDGE,"E80");
            var Q19;
            Q19=sQuery(id+"F19.wireOp",EDGE,"E48");
            var Q20;
            Q20=sQuery(id+"F19.wireOp",EDGE,"E89");
            var Q21;
            Q21=sQuery(id+"F19.wireOp",EDGE,"E82");
            var Q22;
            Q22=sQuery(id+"F19.wireOp",EDGE,"E57");
            var Q23;
            Q23=sQuery(id+"F19.wireOp",EDGE,"E50");
            var Q24;
            Q24=sQuery(id+"F19.wireOp",EDGE,"E66");
            var Q25;
            Q25=sQuery(id+"F19.wireOp",EDGE,"E73");
            var Q26;
            Q26=sQuery(id+"F19.wireOp",EDGE,"E63");
            var Q27;
            Q27=sQuery(id+"F19.wireOp",EDGE,"E79");
            var Q28;
            Q28=sQuery(id+"F19.wireOp",EDGE,"E47");
            var Q29;
            Q29=sQuery(id+"F19.wireOp",EDGE,"E88");
            var Q30;
            Q30=sQuery(id+"F19.wireOp",EDGE,"E40");
            var Q31;
            Q31=sQuery(id+"F19.wireOp",EDGE,"E62");
            var Q32;
            Q32=sQuery(id+"F19.wireOp",EDGE,"E46");
            var Q33;
            Q33=sQuery(id+"F19.wireOp",EDGE,"E78");
            var Q34;
            Q34=sQuery(id+"F19.wireOp",EDGE,"E39");
            var Q35;
            Q35=sQuery(id+"F19.wireOp",EDGE,"E71");
            var Q36;
            Q36=sQuery(id+"F19.wireOp",EDGE,"E77");
            var Q37;
            Q37=sQuery(id+"F19.wireOp",EDGE,"E61");
            var Q38;
            Q38=sQuery(id+"F19.wireOp",EDGE,"E86");
            var Q39;
            Q39=sQuery(id+"F19.wireOp",EDGE,"E54");
            var Q40;
            Q40=sQuery(id+"F19.wireOp",EDGE,"E44");
            var Q41;
            Q41=sQuery(id+"F19.wireOp",EDGE,"E85");
            var Q42;
            Q42=sQuery(id+"F19.wireOp",EDGE,"E37");
            var Q43;
            Q43=sQuery(id+"F19.wireOp",EDGE,"E69");
            var Q44;
            Q44=sQuery(id+"F19.wireOp",EDGE,"E60");
            var Q45;
            Q45=sQuery(id+"F19.wireOp",EDGE,"E76");
            var Q46;
            Q46=sQuery(id+"F19.wireOp",EDGE,"E92");
            var Q47;
            Q47=sQuery(id+"F19.wireOp",EDGE,"E36");
            var Q48;
            Q48=sQuery(id+"F19.wireOp",EDGE,"E68");
            var Q49;
            Q49=sQuery(id+"F19.wireOp",EDGE,"E59");
            var Q50;
            Q50=sQuery(id+"F19.wireOp",EDGE,"E75");
            var Q51;
            Q51=sQuery(id+"F19.wireOp",EDGE,"E91");
            var Q52;
            Q52=sQuery(id+"F19.wireOp",EDGE,"E43");
            var Q53;
            Q53=sQuery(id+"F19.wireOp",EDGE,"E32");
            var Q54;
            Q54=sQuery(id+"F19.wireOp",EDGE,"E28");
            var Q55;
            Q55=sQuery(id+"F19.wireOp",EDGE,"E26");
            var Q56;
            Q56=sQuery(id+"F19.wireOp",EDGE,"E23");
            var Q57;
            Q57=sQuery(id+"F19.wireOp",EDGE,"E21");
            var Q58;
            Q58=sQuery(id+"F19.wireOp",EDGE,"E34");
            var Q59;
            Q59=sQuery(id+"F19.wireOp",EDGE,"E90");
            var Q60;
            Q60=sQuery(id+"F19.wireOp",EDGE,"E41");
            var Q61;
            Q61=sQuery(id+"F19.wireOp",EDGE,"E81");
            var Q62;
            Q62=sQuery(id+"F19.wireOp",EDGE,"E56");
            var Q63;
            Q63=sQuery(id+"F19.wireOp",EDGE,"E49");
            var Q64;
            Q64=sQuery(id+"F19.wireOp",EDGE,"E72");
            var Q65;
            Q65=sQuery(id+"F19.wireOp",EDGE,"E65");
            var Q66;
            Q66=sQuery(id+"F19.wireOp",EDGE,"E87");
            var Q67;
            Q67=sQuery(id+"F19.wireOp",EDGE,"E55");
            var Q68;
            Q68=sQuery(id+"F19.wireOp",EDGE,"E45");
            var Q69;
            Q69=sQuery(id+"F19.wireOp",EDGE,"E38");
            var Q70;
            Q70=sQuery(id+"F19.wireOp",EDGE,"E70");
            var Q71;
            Q71=sQuery(id+"F19.wireOp",EDGE,"E53");
            var Q72;
            Q72=sQuery(id+"F19.wireOp",EDGE,"E84");
            var Q73;
            Q73=sQuery(id+"F19.wireOp",EDGE,"E52");
            extrude(context, id + "F20", {"entities" : qUnion([Q0]), "operationType" : NewBodyOperationType.REMOVE, "surfaceEntities" : qUnion([Q1, Q2, Q3, Q4, Q5, Q6, Q7, Q8, Q9, Q10, Q11, Q12, Q13, Q14, Q15, Q16, Q17, Q18, Q19, Q20, Q21, Q22, Q23, Q24, Q25, Q26, Q27, Q28, Q29, Q30, Q31, Q32, Q33, Q34, Q35, Q36, Q37, Q38, Q39, Q40, Q41, Q42, Q43, Q44, Q45, Q46, Q47, Q48, Q49, Q50, Q51, Q52, Q53, Q54, Q55, Q56, Q57, Q58, Q59, Q60, Q61, Q62, Q63, Q64, Q65, Q66, Q67, Q68, Q69, Q70, Q71, Q72, Q73]), "oppositeDirection" : true, "depth" : 2.54 * mm, "offsetDistance" : 25.4 * mm});
        }
    });
